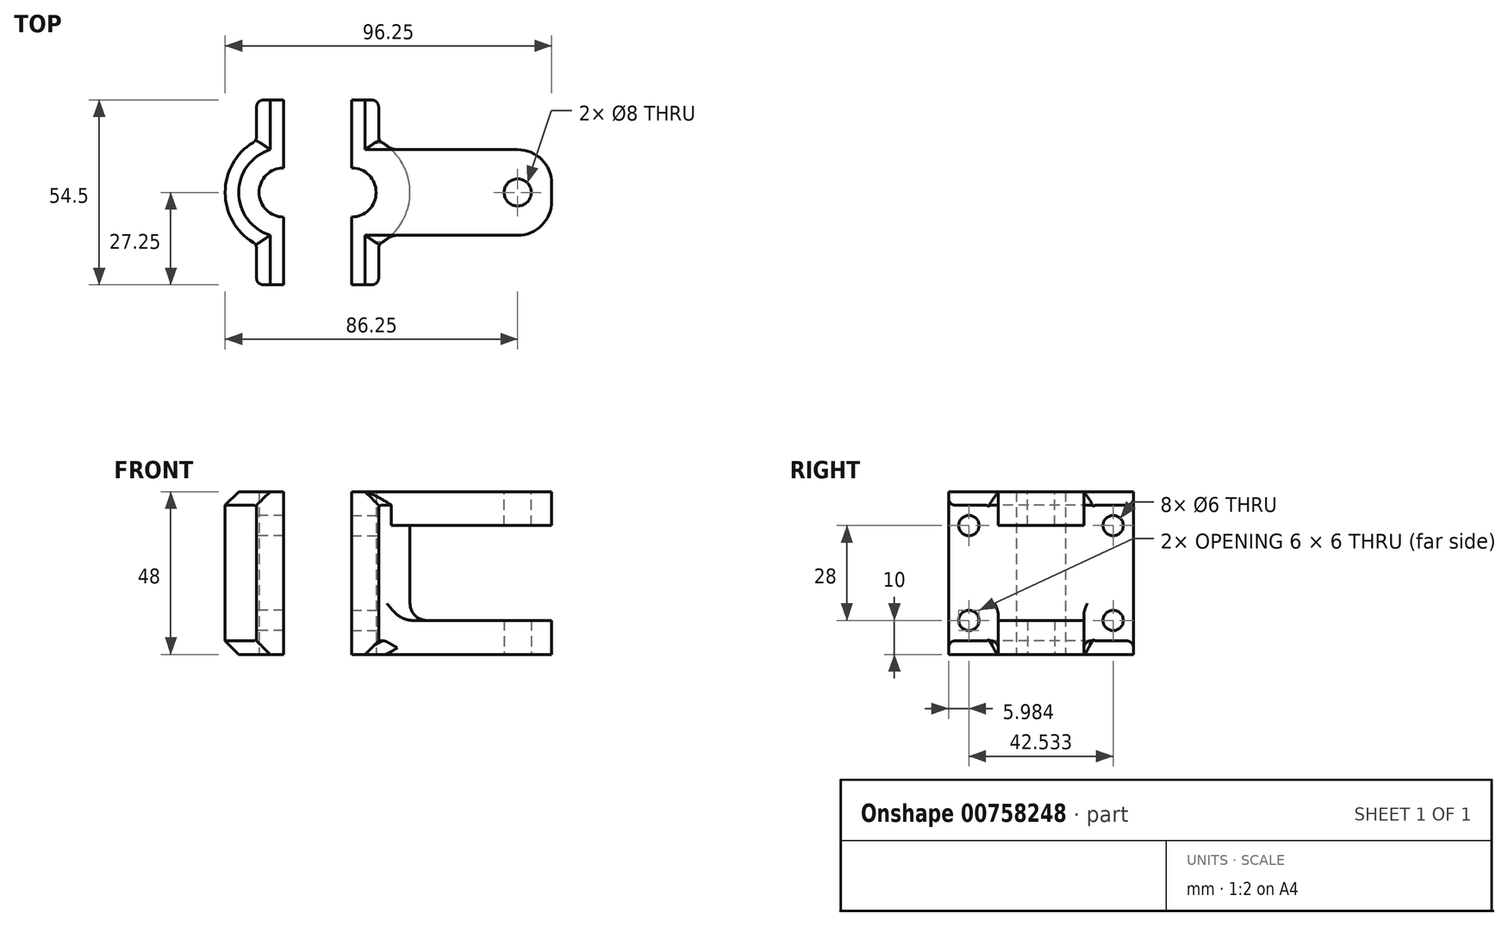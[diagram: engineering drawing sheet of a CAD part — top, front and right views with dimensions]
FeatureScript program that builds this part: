
annotation { "Feature Type Name" : "Feature", "Feature Type Description" : "" }
export const myFeature = defineFeature(function(context is Context, id is Id, definition is map)
    precondition{}
    {
        {
            var Q0;
            Q0=qCreatedBy(makeId("Top.planeOp"),FACE);
            var sketch = newSketch(context, id + "F0", { "sketchPlane" : qUnion([Q0])});
            skArc(sketch, "E0", {"start": v(0, -7.25) * mm, "mid": v(-7.25, 0) * mm, "end": v(0, 7.25) * mm});
            skLineSegment(sketch, "E1", {"start": v(0, 7.25) * mm, "end": v(0, 27.25) * mm});
            skLineSegment(sketch, "E2", {"start": v(0, 27.25) * mm, "end": v(-8, 27.25) * mm});
            skLineSegment(sketch, "E3", {"start": v(-8, 27.25) * mm, "end": v(-8, 15.28) * mm});
            skLineSegment(sketch, "E4.MirrorCS", {"start": v(0, -7.25) * mm, "end": v(0, -27.25) * mm});
            skLineSegment(sketch, "E5.MirrorCS", {"start": v(0, -27.25) * mm, "end": v(-8, -27.25) * mm});
            skLineSegment(sketch, "E6.MirrorCS", {"start": v(-8, -27.25) * mm, "end": v(-8, -15.28) * mm});
            skArc(sketch, "E7", {"start": v(-8, -15.28) * mm, "mid": v(-17.25, 0) * mm, "end": v(-8, 15.28) * mm});
            skSolve(sketch);
        }
        {
            var Q0;
            Q0 = qSketchRegion(id + "F0", true);
            extrude(context, id + "F1", {"entities" : qUnion([Q0]), "depth" : 48 * mm, "offsetDistance" : 25 * mm});
        }
        {
            var Q0;
            Q0=makeQuery(id+"F1.opExtrude","SWEPT_FACE",FACE,{"disambiguationData":[OSD([sQuery(id+"F0.wireOp",EDGE,"E6.MirrorCS")])]});
            var sketch = newSketch(context, id + "F2", { "sketchPlane" : qUnion([Q0])});
            skLineSegment(sketch, "E8", {"start": v(21.27, 48) * mm, "end": v(21.27, 38) * mm, "construction": true});
            skLineSegment(sketch, "E9", {"start": v(21.27, 0) * mm, "end": v(21.27, 10) * mm, "construction": true});
            skLineSegment(sketch, "E10.MirrorCS", {"start": v(-21.27, 48) * mm, "end": v(-21.27, 38) * mm, "construction": true});
            skLineSegment(sketch, "E11.MirrorCS", {"start": v(-21.27, 0) * mm, "end": v(-21.27, 10) * mm, "construction": true});
            skSolve(sketch);
        }
        {
            var Q0;
            Q0=sQuery(id+"F2.wireOp",VERTEX,"E8.end");
            var Q1;
            Q1=sQuery(id+"F2.wireOp",VERTEX,"E9.end");
            var Q2;
            Q2=sQuery(id+"F2.wireOp",VERTEX,"E10.MirrorCS.end");
            var Q3;
            Q3=sQuery(id+"F2.wireOp",VERTEX,"E11.MirrorCS.end");
            var Q4;
            Q4=makeQuery(id+"F1.opExtrude","SWEPT_BODY",BODY,{"disambiguationData":[OSD([sQuery(id+"F0.wireOp",EDGE,"E0"),sQuery(id+"F0.wireOp",EDGE,"E1"),sQuery(id+"F0.wireOp",EDGE,"E2"),sQuery(id+"F0.wireOp",EDGE,"E3"),sQuery(id+"F0.wireOp",EDGE,"E4.MirrorCS"),sQuery(id+"F0.wireOp",EDGE,"E5.MirrorCS"),sQuery(id+"F0.wireOp",EDGE,"E6.MirrorCS"),sQuery(id+"F0.wireOp",EDGE,"E7")])]});
            hole(context, id + "F3", {"style" : HoleStyle.SIMPLE, "endStyle" : HoleEndStyle.THROUGH, "holeDiameter" : 6 * mm, "majorDiameter" : 5 * mm, "isTappedThrough" : true, "tappedDepth" : 12 * mm, "tapClearance" : 3, "locations" : qUnion([Q0, Q1, Q2, Q3]), "scope" : qUnion([Q4])});
        }
        {
            var Q0;
            Q0=makeQuery(id+"F1.opExtrude","CAP_EDGE",EDGE,{"disambiguationData":[OSD([sQuery(id+"F0.wireOp",EDGE,"E7")])],"isStart":true});
            var Q1;
            Q1=makeQuery(id+"F1.opExtrude","CAP_EDGE",EDGE,{"disambiguationData":[OSD([sQuery(id+"F0.wireOp",EDGE,"E3")])],"isStart":true});
            var Q2;
            Q2=makeQuery(id+"F1.opExtrude","CAP_EDGE",EDGE,{"disambiguationData":[OSD([sQuery(id+"F0.wireOp",EDGE,"E6.MirrorCS")])],"isStart":true});
            var Q3;
            Q3=makeQuery(id+"F1.opExtrude","CAP_EDGE",EDGE,{"disambiguationData":[OSD([sQuery(id+"F0.wireOp",EDGE,"E3")])],"isStart":false});
            var Q4;
            Q4=makeQuery(id+"F1.opExtrude","CAP_EDGE",EDGE,{"disambiguationData":[OSD([sQuery(id+"F0.wireOp",EDGE,"E7")])],"isStart":false});
            var Q5;
            Q5=makeQuery(id+"F1.opExtrude","CAP_EDGE",EDGE,{"disambiguationData":[OSD([sQuery(id+"F0.wireOp",EDGE,"E6.MirrorCS")])],"isStart":false});
            chamfer(context, id + "F4", {"entities" : qUnion([Q0, Q1, Q2, Q3, Q4, Q5]), "width" : 4 * mm, "tangentPropagation" : true});
        }
        {
            var Q0;
            Q0=makeQuery(id+"F1.opExtrude","SWEPT_EDGE",EDGE,{"disambiguationData":[OSD([sQuery(id+"F0.wireOp",EDGE,"E3"),sQuery(id+"F0.wireOp",EDGE,"E7")])]});
            var Q1;
            Q1=makeQuery(id+"F1.opExtrude","SWEPT_EDGE",EDGE,{"disambiguationData":[OSD([sQuery(id+"F0.wireOp",EDGE,"E6.MirrorCS"),sQuery(id+"F0.wireOp",EDGE,"E7")])]});
            var Q2;
            Q2=makeQuery(id+"F1.opExtrude","SWEPT_EDGE",EDGE,{"disambiguationData":[OSD([sQuery(id+"F0.wireOp",EDGE,"E2"),sQuery(id+"F0.wireOp",EDGE,"E3")])]});
            var Q3;
            Q3=makeQuery(id+"F1.opExtrude","SWEPT_EDGE",EDGE,{"disambiguationData":[OSD([sQuery(id+"F0.wireOp",EDGE,"E5.MirrorCS"),sQuery(id+"F0.wireOp",EDGE,"E6.MirrorCS")])]});
            fillet(context, id + "F5", {"entities" : qUnion([Q0, Q1, Q2, Q3]), "radius" : 2 * mm, "tangentPropagation" : true, "allowEdgeOverflow" : false});
        }
        {
            var Q0;
            Q0=qCreatedBy(makeId("Right.planeOp"),FACE);
            cPlane(context, id + "F6", {"entities" : qUnion([Q0]), "cplaneType" : CPlaneType.OFFSET, "offset" : 10 * mm, "width" : 150 * mm, "height" : 150 * mm});
        }
        {
            var Q0;
            Q0=makeQuery(id+"F1.opExtrude","SWEPT_BODY",BODY,{"disambiguationData":[OSD([sQuery(id+"F0.wireOp",EDGE,"E0"),sQuery(id+"F0.wireOp",EDGE,"E1"),sQuery(id+"F0.wireOp",EDGE,"E2"),sQuery(id+"F0.wireOp",EDGE,"E3"),sQuery(id+"F0.wireOp",EDGE,"E4.MirrorCS"),sQuery(id+"F0.wireOp",EDGE,"E5.MirrorCS"),sQuery(id+"F0.wireOp",EDGE,"E6.MirrorCS"),sQuery(id+"F0.wireOp",EDGE,"E7")])]});
            var Q1;
            Q1=qCreatedBy(id+"F6.planeOp",FACE);
            mirror(context, id + "F7", {"entities" : qUnion([Q0]), "mirrorPlane" : qUnion([Q1])});
        }
        {
            var Q0;
            Q0=makeQuery(id+"F7.opPattern","COPY",FACE,{"derivedFrom":makeQuery(id+"F1.opExtrude","CAP_FACE",FACE,{"disambiguationData":[OSD([sQuery(id+"F0.wireOp",EDGE,"E0"),sQuery(id+"F0.wireOp",EDGE,"E1"),sQuery(id+"F0.wireOp",EDGE,"E2"),sQuery(id+"F0.wireOp",EDGE,"E3"),sQuery(id+"F0.wireOp",EDGE,"E4.MirrorCS"),sQuery(id+"F0.wireOp",EDGE,"E5.MirrorCS"),sQuery(id+"F0.wireOp",EDGE,"E6.MirrorCS"),sQuery(id+"F0.wireOp",EDGE,"E7")])],"isStart":true}),"instanceName":"1"});
            var sketch = newSketch(context, id + "F8", { "sketchPlane" : qUnion([Q0])});
            skLineSegment(sketch, "E12.bottom", {"start": v(24, 12.63) * mm, "end": v(79, 12.63) * mm});
            skLineSegment(sketch, "E12.top", {"start": v(24, -12.63) * mm, "end": v(79, -12.63) * mm});
            skLineSegment(sketch, "E12.left", {"start": v(24, 12.63) * mm, "end": v(24, 6.05) * mm});
            skLineSegment(sketch, "E12.right", {"start": v(79, 12.63) * mm, "end": v(79, -12.63) * mm});
            skArc(sketch, "E13", {"start": v(24, 6.05) * mm, "mid": v(27.25, 0) * mm, "end": v(24, -6.05) * mm});
            skLineSegment(sketch, "E14.trimOffspring", {"start": v(24, -6.05) * mm, "end": v(24, -12.63) * mm});
            skLineSegment(sketch, "E15", {"start": v(79, 0) * mm, "end": v(69, 0) * mm, "construction": true});
            skCircle(sketch, "E16", {"center": v(69, 0) * mm, "radius": 4 * mm});
            skSolve(sketch);
        }
        {
            var Q0;
            Q0 = qSketchRegion(id + "F8", true);
            extrude(context, id + "F9", {"entities" : qUnion([Q0]), "operationType" : NewBodyOperationType.ADD, "oppositeDirection" : true, "depth" : 10 * mm, "offsetDistance" : 25 * mm});
        }
        {
            var Q0;
            Q0=makeQuery(id+"F9.boolean.opBoolean","INTERSECT",EDGE,{"derivedFrom":[makeQuery(id+"F7.opPattern","COPY",FACE,{"derivedFrom":makeQuery(id+"F1.opExtrude","SWEPT_FACE",FACE,{"disambiguationData":[OSD([sQuery(id+"F0.wireOp",EDGE,"E7")])]}),"instanceName":"1"}),makeQuery(id+"F9.opExtrude","SWEPT_FACE",FACE,{"disambiguationData":[OSD([sQuery(id+"F8.wireOp",EDGE,"E12.bottom")])]})]});
            var Q1;
            {var subQ0=sQuery(id+"F0.wireOp",EDGE,"E7");Q1=makeQuery(id+"F9.boolean.opBoolean","INTERSECT",EDGE,{"derivedFrom":[makeQuery(id+"F7.opPattern","COPY",FACE,{"derivedFrom":makeQuery(id+"F4.opChamfer","BLEND_FACE",FACE,{"disambiguationData":[OSD([subQ0]),TDD([makeQuery(id+"F1.opExtrude","CAP_EDGE",EDGE,{"disambiguationData":[OSD([subQ0])],"isStart":true})])]}),"instanceName":"1"}),makeQuery(id+"F9.opExtrude","SWEPT_FACE",FACE,{"disambiguationData":[OSD([sQuery(id+"F8.wireOp",EDGE,"E12.bottom")])]})]});}
            var Q2;
            Q2=makeQuery(id+"F9.boolean.opBoolean","INTERSECT",EDGE,{"derivedFrom":[makeQuery(id+"F7.opPattern","COPY",FACE,{"derivedFrom":makeQuery(id+"F1.opExtrude","SWEPT_FACE",FACE,{"disambiguationData":[OSD([sQuery(id+"F0.wireOp",EDGE,"E7")])]}),"instanceName":"1"}),makeQuery(id+"F9.opExtrude","SWEPT_FACE",FACE,{"disambiguationData":[OSD([sQuery(id+"F8.wireOp",EDGE,"E12.top")])]})]});
            var Q3;
            {var subQ0=sQuery(id+"F0.wireOp",EDGE,"E7");Q3=makeQuery(id+"F9.boolean.opBoolean","INTERSECT",EDGE,{"derivedFrom":[makeQuery(id+"F7.opPattern","COPY",FACE,{"derivedFrom":makeQuery(id+"F4.opChamfer","BLEND_FACE",FACE,{"disambiguationData":[OSD([subQ0]),TDD([makeQuery(id+"F1.opExtrude","CAP_EDGE",EDGE,{"disambiguationData":[OSD([subQ0])],"isStart":true})])]}),"instanceName":"1"}),makeQuery(id+"F9.opExtrude","SWEPT_FACE",FACE,{"disambiguationData":[OSD([sQuery(id+"F8.wireOp",EDGE,"E12.top")])]})]});}
            var Q4;
            Q4=makeQuery(id+"F9.boolean.opBoolean","INTERSECT",EDGE,{"derivedFrom":[makeQuery(id+"F7.opPattern","COPY",FACE,{"derivedFrom":makeQuery(id+"F1.opExtrude","SWEPT_FACE",FACE,{"disambiguationData":[OSD([sQuery(id+"F0.wireOp",EDGE,"E7")])]}),"instanceName":"1"}),makeQuery(id+"F9.opExtrude","CAP_FACE",FACE,{"disambiguationData":[OSD([sQuery(id+"F8.wireOp",EDGE,"E12.bottom"),sQuery(id+"F8.wireOp",EDGE,"E12.top"),sQuery(id+"F8.wireOp",EDGE,"E12.left"),sQuery(id+"F8.wireOp",EDGE,"E12.right"),sQuery(id+"F8.wireOp",EDGE,"E13"),sQuery(id+"F8.wireOp",EDGE,"E14.trimOffspring"),sQuery(id+"F8.wireOp",EDGE,"E16")])],"isStart":false})]});
            fillet(context, id + "F10", {"entities" : qUnion([Q0, Q1, Q2, Q3, Q4]), "radius" : 5 * mm, "tangentPropagation" : true, "allowEdgeOverflow" : false});
        }
        {
            var Q0;
            Q0=makeQuery(id+"F9.opExtrude","SWEPT_EDGE",EDGE,{"disambiguationData":[OSD([sQuery(id+"F8.wireOp",EDGE,"E12.bottom"),sQuery(id+"F8.wireOp",EDGE,"E12.right")])]});
            var Q1;
            Q1=makeQuery(id+"F9.opExtrude","SWEPT_EDGE",EDGE,{"disambiguationData":[OSD([sQuery(id+"F8.wireOp",EDGE,"E12.top"),sQuery(id+"F8.wireOp",EDGE,"E12.right")])]});
            fillet(context, id + "F11", {"entities" : qUnion([Q0, Q1]), "radius" : 10 * mm, "tangentPropagation" : true, "allowEdgeOverflow" : false});
        }
        {
            var Q0;
            Q0=makeQuery(id+"F7.opPattern","COPY",FACE,{"derivedFrom":makeQuery(id+"F1.opExtrude","CAP_FACE",FACE,{"disambiguationData":[OSD([sQuery(id+"F0.wireOp",EDGE,"E0"),sQuery(id+"F0.wireOp",EDGE,"E1"),sQuery(id+"F0.wireOp",EDGE,"E2"),sQuery(id+"F0.wireOp",EDGE,"E3"),sQuery(id+"F0.wireOp",EDGE,"E4.MirrorCS"),sQuery(id+"F0.wireOp",EDGE,"E5.MirrorCS"),sQuery(id+"F0.wireOp",EDGE,"E6.MirrorCS"),sQuery(id+"F0.wireOp",EDGE,"E7")])],"isStart":false}),"instanceName":"1"});
            var sketch = newSketch(context, id + "F12", { "sketchPlane" : qUnion([Q0])});
            skLineSegment(sketch, "E17", {"start": v(24, 12.63) * mm, "end": v(69, 12.63) * mm});
            skLineSegment(sketch, "E18", {"start": v(79, 2.63) * mm, "end": v(79, -2.63) * mm});
            skLineSegment(sketch, "E19", {"start": v(69, -12.63) * mm, "end": v(24, -12.63) * mm});
            skLineSegment(sketch, "E20", {"start": v(24, -12.63) * mm, "end": v(24, -6.05) * mm});
            skLineSegment(sketch, "E21", {"start": v(24, 12.63) * mm, "end": v(24, 6.05) * mm});
            skArc(sketch, "E22", {"start": v(24, 6.05) * mm, "mid": v(27.25, 0) * mm, "end": v(24, -6.05) * mm});
            skPoint(sketch, "E23.visualSharp", {"position": v(79, 12.63) * mm});
            skArc(sketch, "E23.filletArc", {"start": v(79, 2.63) * mm, "mid": v(76.07, 9.7) * mm, "end": v(69, 12.63) * mm});
            skPoint(sketch, "E24.visualSharp", {"position": v(79, -12.63) * mm});
            skArc(sketch, "E24.filletArc", {"start": v(69, -12.63) * mm, "mid": v(76.07, -9.7) * mm, "end": v(79, -2.63) * mm});
            skLineSegment(sketch, "E25", {"start": v(79, 0) * mm, "end": v(69, 0) * mm, "construction": true});
            skCircle(sketch, "E26", {"center": v(69, 0) * mm, "radius": 4 * mm});
            skSolve(sketch);
        }
        {
            var Q0;
            Q0 = qSketchRegion(id + "F12", true);
            extrude(context, id + "F13", {"entities" : qUnion([Q0]), "operationType" : NewBodyOperationType.ADD, "oppositeDirection" : true, "depth" : 10 * mm, "offsetDistance" : 25 * mm});
        }
    });
